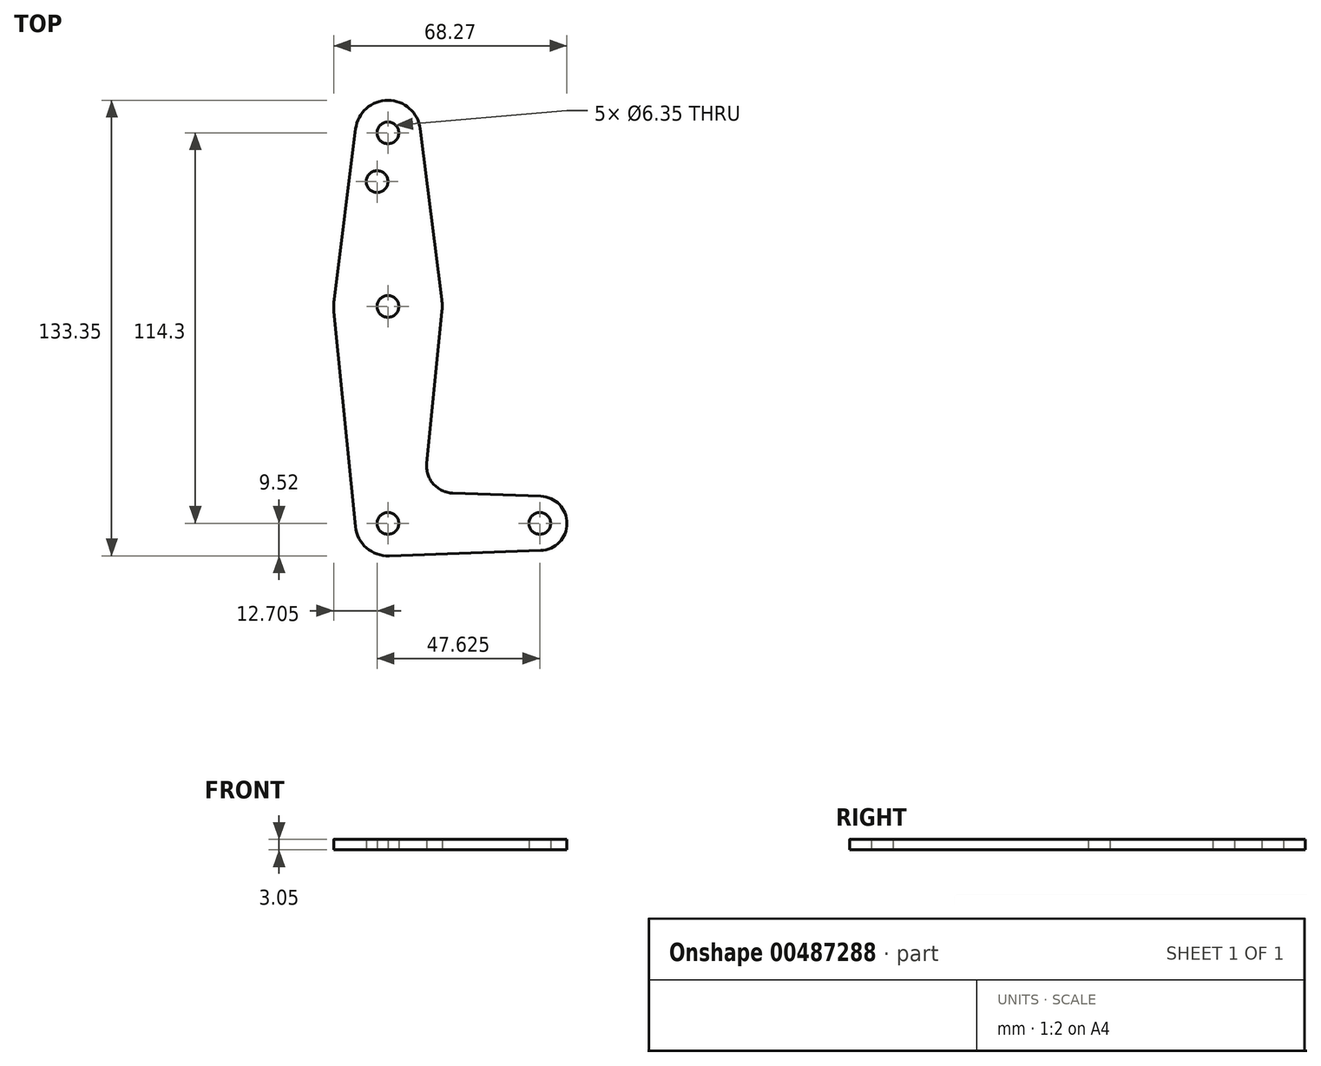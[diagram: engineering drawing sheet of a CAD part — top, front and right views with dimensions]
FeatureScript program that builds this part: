
annotation { "Feature Type Name" : "Feature", "Feature Type Description" : "" }
export const myFeature = defineFeature(function(context is Context, id is Id, definition is map)
    precondition{}
    {
        {
            var Q0;
            Q0=qCreatedBy(makeId("Top.planeOp"),FACE);
            var sketch = newSketch(context, id + "F0", { "sketchPlane" : qUnion([Q0])});
            skLineSegment(sketch, "E0", {"start": v(0, 0) * mm, "end": v(0, 114.3) * mm, "construction": true});
            skLineSegment(sketch, "E1", {"start": v(0, 0) * mm, "end": v(44.45, 0) * mm, "construction": true});
            skCircle(sketch, "E2", {"center": v(0, 114.3) * mm, "radius": 9.53 * mm});
            skCircle(sketch, "E3", {"center": v(44.45, 0) * mm, "radius": 7.94 * mm});
            skCircle(sketch, "E4", {"center": v(0, 63.5) * mm, "radius": 15.88 * mm});
            skCircle(sketch, "E5", {"center": v(0, 0) * mm, "radius": 9.53 * mm});
            skLineSegment(sketch, "E6", {"start": v(9.45, 115.5) * mm, "end": v(15.75, 65.48) * mm});
            skLineSegment(sketch, "E7", {"start": v(-9.45, 115.5) * mm, "end": v(-15.75, 65.48) * mm});
            skLineSegment(sketch, "E8", {"start": v(15.8, 61.91) * mm, "end": v(11.34, 17.6) * mm});
            skLineSegment(sketch, "E9", {"start": v(-15.8, 61.91) * mm, "end": v(-9.48, -0.95) * mm});
            skLineSegment(sketch, "E10", {"start": v(0.34, -9.52) * mm, "end": v(44.73, -7.93) * mm});
            skLineSegment(sketch, "E11", {"start": v(18.97, 8.85) * mm, "end": v(44.73, 7.93) * mm});
            skCircle(sketch, "E12", {"center": v(0, 114.3) * mm, "radius": 3.18 * mm});
            skCircle(sketch, "E13", {"center": v(0, 63.5) * mm, "radius": 3.18 * mm});
            skCircle(sketch, "E14", {"center": v(0, 0) * mm, "radius": 3.18 * mm});
            skCircle(sketch, "E15", {"center": v(44.45, 0) * mm, "radius": 3.18 * mm});
            skCircle(sketch, "E16", {"center": v(-3.18, 100.03) * mm, "radius": 3.18 * mm});
            skArc(sketch, "E17.filletArc", {"start": v(11.34, 17.6) * mm, "mid": v(13.26, 11.57) * mm, "end": v(18.97, 8.85) * mm});
            skSolve(sketch);
        }
        {
            var Q0;
            Q0 = qSketchRegion(id + "F0", true);
            extrude(context, id + "F1", {"entities" : qUnion([Q0]), "depth" : 3.05 * mm});
        }
    });
